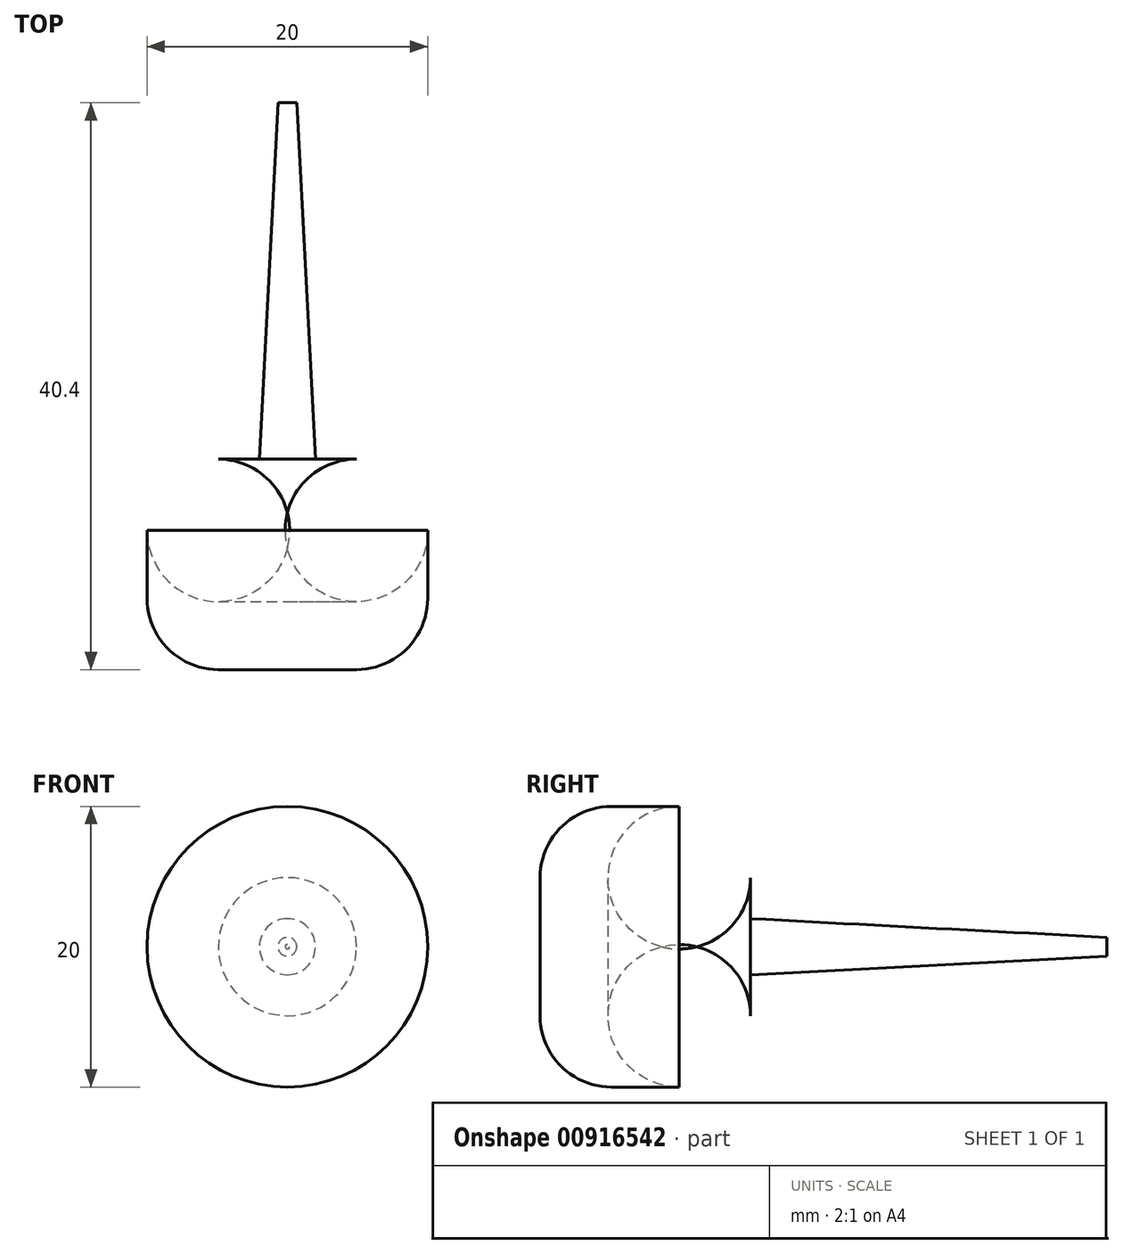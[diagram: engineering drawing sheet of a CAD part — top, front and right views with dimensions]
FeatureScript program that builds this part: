
annotation { "Feature Type Name" : "Feature", "Feature Type Description" : "" }
export const myFeature = defineFeature(function(context is Context, id is Id, definition is map)
    precondition{}
    {
        {
            var Q0;
            Q0=qCreatedBy(makeId("Front.planeOp"),FACE);
            var sketch = newSketch(context, id + "F0", { "sketchPlane" : qUnion([Q0])});
            skCircle(sketch, "E0", {"center": v(0, 0) * mm, "radius": 10 * mm});
            skSolve(sketch);
        }
        {
            var Q0;
            Q0 = qSketchRegion(id + "F0", true);
            extrude(context, id + "F1", {"entities" : qUnion([Q0]), "oppositeDirection" : true, "depth" : 15 * mm, "offsetDistance" : 25.4 * mm});
        }
        {
            var Q0;
            Q0=makeQuery(id+"F1.opExtrude","CAP_EDGE",EDGE,{"disambiguationData":[OSD([sQuery(id+"F0.wireOp",EDGE,"E0")])],"isStart":true});
            var Q1;
            Q1=makeQuery(id+"F1.opExtrude","CAP_EDGE",EDGE,{"disambiguationData":[OSD([sQuery(id+"F0.wireOp",EDGE,"E0")])],"isStart":false});
            fillet(context, id + "F2", {"entities" : qUnion([Q0, Q1]), "radius" : 5.08 * mm, "tangentPropagation" : true, "allowEdgeOverflow" : false});
        }
        {
            var Q0;
            Q0=makeQuery(id+"F1.opExtrude","CAP_FACE",FACE,{"disambiguationData":[OSD([sQuery(id+"F0.wireOp",EDGE,"E0")])],"isStart":false});
            var sketch = newSketch(context, id + "F3", { "sketchPlane" : qUnion([Q0])});
            skCircle(sketch, "E1", {"center": v(0, 0) * mm, "radius": 2 * mm});
            skSolve(sketch);
        }
        {
            var Q0;
            Q0 = qSketchRegion(id + "F3", true);
            extrude(context, id + "F4", {"entities" : qUnion([Q0]), "operationType" : NewBodyOperationType.ADD, "depth" : 25.4 * mm, "offsetDistance" : 25.4 * mm, "hasDraft" : true, "draftAngle" : 3 * degree, "draftPullDirection" : true});
        }
    });
